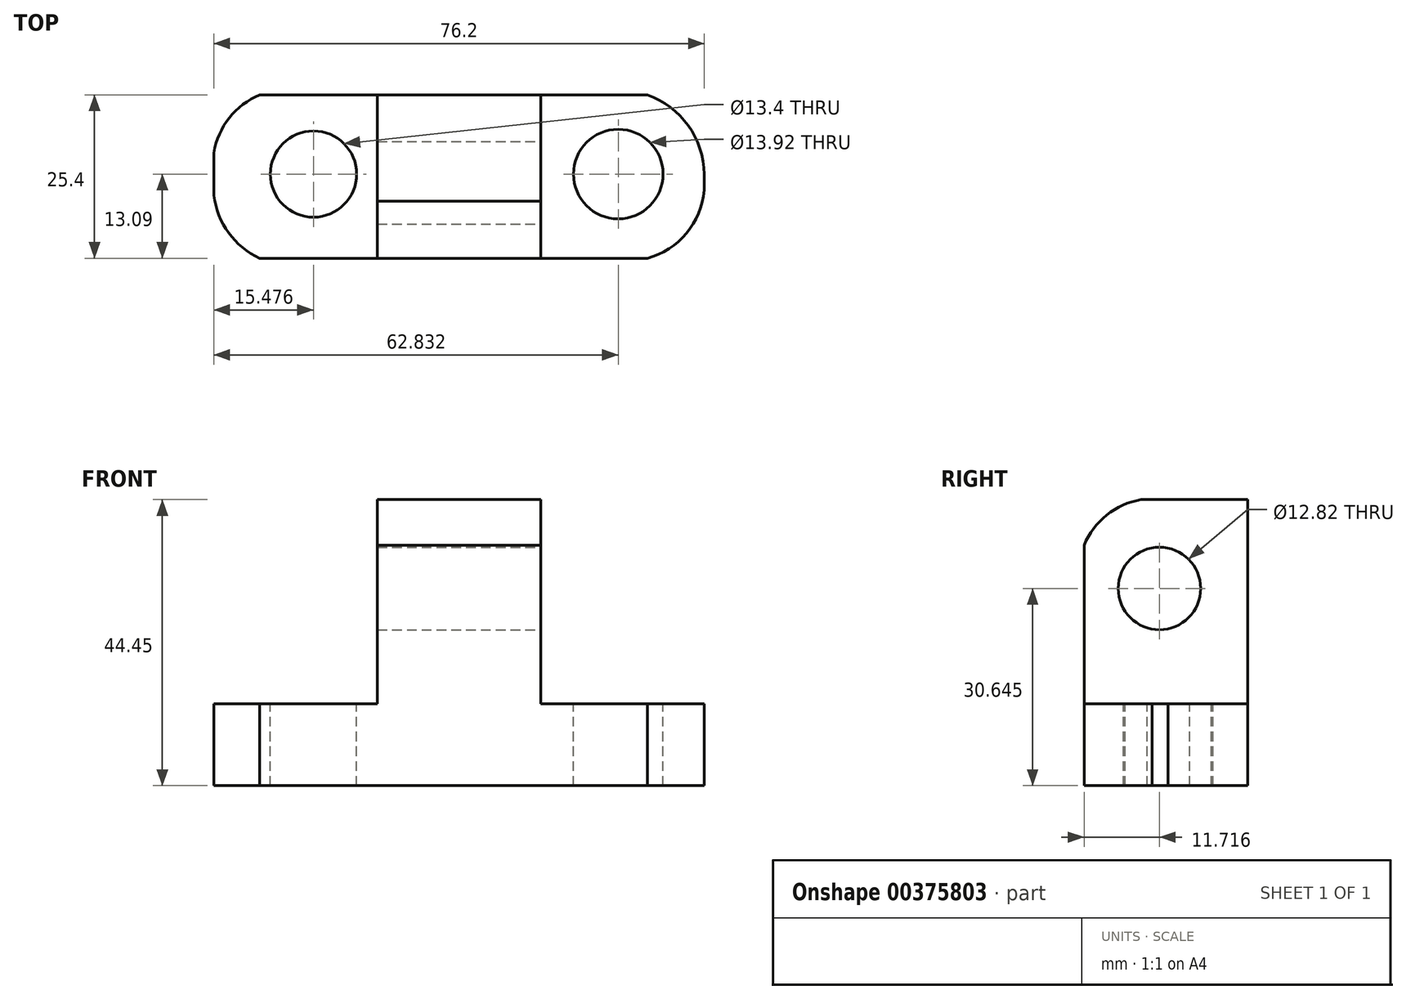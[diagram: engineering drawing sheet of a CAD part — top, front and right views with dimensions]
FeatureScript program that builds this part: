
annotation { "Feature Type Name" : "Feature", "Feature Type Description" : "" }
export const myFeature = defineFeature(function(context is Context, id is Id, definition is map)
    precondition{}
    {
        {
            var Q0;
            Q0=qCreatedBy(makeId("Front.planeOp"),FACE);
            var sketch = newSketch(context, id + "F0", { "sketchPlane" : qUnion([Q0])});
            skLineSegment(sketch, "E0", {"start": v(0, 0) * mm, "end": v(76.2, 0) * mm});
            skLineSegment(sketch, "E1", {"start": v(76.2, 0) * mm, "end": v(76.2, 44.45) * mm});
            skLineSegment(sketch, "E2", {"start": v(76.2, 44.45) * mm, "end": v(0, 44.45) * mm});
            skLineSegment(sketch, "E3", {"start": v(0, 44.45) * mm, "end": v(0, 0) * mm});
            skSolve(sketch);
        }
        {
            var Q0;
            Q0 = qSketchRegion(id + "F0", true);
            var Q1;
            Q1=makeQuery(id+"F0.imprint","IMPRINT",FACE,{"disambiguationData":[TD([[makeQuery(id+"F0.imprint","IMPRINT",EDGE,{"derivedFrom":sQuery(id+"F0.wireOp",EDGE,"E0")}),1.0]])]});
            extrude(context, id + "F1", {"entities" : qUnion([Q0, Q1]), "depth" : 25.4 * mm});
        }
        {
            var Q0;
            Q0=makeQuery(id+"F1.opExtrude","CAP_FACE",FACE,{"disambiguationData":[OSD([sQuery(id+"F0.wireOp",EDGE,"E0"),sQuery(id+"F0.wireOp",EDGE,"E1"),sQuery(id+"F0.wireOp",EDGE,"E2"),sQuery(id+"F0.wireOp",EDGE,"E3")])],"isStart":false});
            var sketch = newSketch(context, id + "F2", { "sketchPlane" : qUnion([Q0])});
            skLineSegment(sketch, "E4", {"start": v(0, 12.7) * mm, "end": v(25.4, 12.7) * mm});
            skLineSegment(sketch, "E5", {"start": v(0, 12.7) * mm, "end": v(0, 44.45) * mm});
            skLineSegment(sketch, "E6", {"start": v(0, 44.45) * mm, "end": v(25.4, 44.45) * mm});
            skLineSegment(sketch, "E7", {"start": v(25.4, 44.45) * mm, "end": v(25.4, 12.7) * mm});
            skLineSegment(sketch, "E8", {"start": v(76.2, 12.7) * mm, "end": v(50.8, 12.7) * mm});
            skLineSegment(sketch, "E9", {"start": v(50.8, 12.7) * mm, "end": v(50.8, 44.45) * mm});
            skLineSegment(sketch, "E10", {"start": v(50.8, 44.45) * mm, "end": v(76.2, 44.45) * mm});
            skLineSegment(sketch, "E11", {"start": v(76.2, 44.45) * mm, "end": v(76.2, 12.7) * mm});
            skSolve(sketch);
        }
        {
            var Q0;
            Q0=makeQuery(id+"F2.imprint","IMPRINT",FACE,{"disambiguationData":[TD([[makeQuery(id+"F2.imprint","IMPRINT",EDGE,{"derivedFrom":sQuery(id+"F2.wireOp",EDGE,"E4")}),1.0]])]});
            var Q1;
            Q1=makeQuery(id+"F2.imprint","IMPRINT",FACE,{"disambiguationData":[TD([[makeQuery(id+"F2.imprint","IMPRINT",EDGE,{"derivedFrom":sQuery(id+"F2.wireOp",EDGE,"E8")}),-1.0]])]});
            extrude(context, id + "F3", {"entities" : qUnion([Q0, Q1]), "operationType" : NewBodyOperationType.REMOVE, "oppositeDirection" : true, "depth" : 25.4 * mm});
        }
        {
            var Q0;
            Q0=makeQuery(id+"F3.boolean.opBoolean","COPY",FACE,{"derivedFrom":makeQuery(id+"F3.opExtrude","SWEPT_FACE",FACE,{"disambiguationData":[OSD([sQuery(id+"F2.wireOp",EDGE,"E9")])]})});
            var sketch = newSketch(context, id + "F4", { "sketchPlane" : qUnion([Q0])});
            skArc(sketch, "E12", {"start": v(-12.7, 44.45) * mm, "mid": v(-23.7, 40.24) * mm, "end": v(-25.4, 28.58) * mm});
            skArc(sketch, "E13", {"start": v(0, 28.58) * mm, "mid": v(-2.88, 39.3) * mm, "end": v(-12.7, 44.45) * mm});
            skSolve(sketch);
        }
        {
            var Q0;
            Q0 = qSketchRegion(id + "F4", true);
            var Q1;
            {var subQ0=sQuery(id+"F4.wireOp",EDGE,"E12");var subQ1=sQuery(id+"F2.wireOp",EDGE,"E9");var subQ4=makeQuery(id+"F3.boolean.opBoolean","COPY",EDGE,{"derivedFrom":makeQuery(id+"F3.opExtrude","CAP_EDGE",EDGE,{"disambiguationData":[OSD([subQ1])],"isStart":true})});var subQ5=makeQuery(id+"F4.imprint","INTERSECT",VERTEX,{"disambiguationData":[OD(1.0)],"derivedFrom":[subQ4,subQ0]});Q1=makeQuery(id+"F4.imprint","IMPRINT",FACE,{"disambiguationData":[TD([[makeQuery(id+"F4.imprint","IMPRINT",EDGE,{"disambiguationData":[TD([[subQ5,1.0]])],"derivedFrom":subQ0}),-1.0]])]});}
            var Q2;
            {var subQ0=sQuery(id+"F4.wireOp",EDGE,"E13");var subQ1=sQuery(id+"F2.wireOp",EDGE,"E9");var subQ4=makeQuery(id+"F3.boolean.opBoolean","COPY",EDGE,{"derivedFrom":makeQuery(id+"F3.opExtrude","CAP_EDGE",EDGE,{"disambiguationData":[OSD([subQ1])],"isStart":false})});var subQ5=makeQuery(id+"F4.imprint","INTERSECT",VERTEX,{"disambiguationData":[OD(1.0)],"derivedFrom":[subQ4,subQ0]});Q2=makeQuery(id+"F4.imprint","IMPRINT",FACE,{"disambiguationData":[TD([[makeQuery(id+"F4.imprint","IMPRINT",EDGE,{"disambiguationData":[TD([[subQ5,-1.0]])],"derivedFrom":subQ4}),1.0]])]});}
            extrude(context, id + "F5", {"entities" : qUnion([Q0, Q1, Q2]), "operationType" : NewBodyOperationType.REMOVE, "oppositeDirection" : true, "depth" : 25.4 * mm});
        }
        {
            var Q0;
            Q0=makeQuery(id+"F3.boolean.opBoolean","COPY",FACE,{"derivedFrom":makeQuery(id+"F3.opExtrude","SWEPT_FACE",FACE,{"disambiguationData":[OSD([sQuery(id+"F2.wireOp",EDGE,"E9")])]})});
            var sketch = newSketch(context, id + "F6", { "sketchPlane" : qUnion([Q0])});
            skCircle(sketch, "E14", {"center": v(-13.68, 30.65) * mm, "radius": 6.4 * mm});
            skSolve(sketch);
        }
        {
            var Q0;
            Q0=makeQuery(id+"F6.imprint","IMPRINT",FACE,{"disambiguationData":[TD([[makeQuery(id+"F6.imprint","IMPRINT",EDGE,{"derivedFrom":sQuery(id+"F6.wireOp",EDGE,"E14")}),1.0]])]});
            extrude(context, id + "F7", {"entities" : qUnion([Q0]), "operationType" : NewBodyOperationType.REMOVE, "oppositeDirection" : true, "depth" : 25.4 * mm});
        }
        {
            var Q0;
            Q0=makeQuery(id+"F3.boolean.opBoolean","COPY",FACE,{"derivedFrom":makeQuery(id+"F3.opExtrude","SWEPT_FACE",FACE,{"disambiguationData":[OSD([sQuery(id+"F2.wireOp",EDGE,"E4")])]})});
            var sketch = newSketch(context, id + "F8", { "sketchPlane" : qUnion([Q0])});
            skArc(sketch, "E15", {"start": v(0, -12.7) * mm, "mid": v(1.5, -20.2) * mm, "end": v(7.12, -25.4) * mm});
            skArc(sketch, "E16", {"start": v(7.12, 0) * mm, "mid": v(1.35, -5.11) * mm, "end": v(0, -12.7) * mm});
            skPoint(sketch, "E16.startSnap0", {"position": v(12.7, 0) * mm});
            skSolve(sketch);
        }
        {
            var Q0;
            Q0 = qSketchRegion(id + "F8", true);
            var Q1;
            {var subQ0=sQuery(id+"F8.wireOp",EDGE,"E16");var subQ1=sQuery(id+"F2.wireOp",EDGE,"E4");var subQ2=makeQuery(id+"F3.boolean.opBoolean","COPY",EDGE,{"derivedFrom":makeQuery(id+"F3.opExtrude","CAP_EDGE",EDGE,{"disambiguationData":[OSD([subQ1])],"isStart":false})});var subQ3=makeQuery(id+"F8.imprint","INTERSECT",VERTEX,{"derivedFrom":[subQ2,subQ0]});Q1=makeQuery(id+"F8.imprint","IMPRINT",FACE,{"disambiguationData":[TD([[makeQuery(id+"F8.imprint","IMPRINT",EDGE,{"disambiguationData":[TD([[subQ3,-1.0]])],"derivedFrom":subQ0}),-1.0]])]});}
            var Q2;
            {var subQ0=sQuery(id+"F8.wireOp",EDGE,"E15");var subQ1=sQuery(id+"F2.wireOp",EDGE,"E4");var subQ2=makeQuery(id+"F3.boolean.opBoolean","COPY",EDGE,{"derivedFrom":makeQuery(id+"F3.opExtrude","CAP_EDGE",EDGE,{"disambiguationData":[OSD([subQ1])],"isStart":true})});var subQ3=makeQuery(id+"F8.imprint","INTERSECT",VERTEX,{"derivedFrom":[subQ2,subQ0]});Q2=makeQuery(id+"F8.imprint","IMPRINT",FACE,{"disambiguationData":[TD([[makeQuery(id+"F8.imprint","IMPRINT",EDGE,{"disambiguationData":[TD([[subQ3,1.0]])],"derivedFrom":subQ0}),-1.0]])]});}
            extrude(context, id + "F9", {"entities" : qUnion([Q0, Q1, Q2]), "operationType" : NewBodyOperationType.REMOVE, "oppositeDirection" : true, "depth" : 25.4 * mm});
        }
        {
            var Q0;
            Q0=makeQuery(id+"F3.boolean.opBoolean","COPY",FACE,{"derivedFrom":makeQuery(id+"F3.opExtrude","SWEPT_FACE",FACE,{"disambiguationData":[OSD([sQuery(id+"F2.wireOp",EDGE,"E8")])]})});
            var sketch = newSketch(context, id + "F10", { "sketchPlane" : qUnion([Q0])});
            skArc(sketch, "E17", {"start": v(67.34, -25.4) * mm, "mid": v(74.08, -20.66) * mm, "end": v(76.2, -12.7) * mm});
            skArc(sketch, "E18", {"start": v(76.2, -12.7) * mm, "mid": v(73.81, -4.92) * mm, "end": v(67.34, 0) * mm});
            skSolve(sketch);
        }
        {
            var Q0;
            {var subQ0=sQuery(id+"F10.wireOp",EDGE,"E18");var subQ1=sQuery(id+"F2.wireOp",EDGE,"E8");var subQ2=makeQuery(id+"F3.boolean.opBoolean","COPY",EDGE,{"derivedFrom":makeQuery(id+"F3.opExtrude","CAP_EDGE",EDGE,{"disambiguationData":[OSD([subQ1])],"isStart":false})});var subQ3=makeQuery(id+"F10.imprint","INTERSECT",VERTEX,{"derivedFrom":[subQ2,subQ0]});Q0=makeQuery(id+"F10.imprint","IMPRINT",FACE,{"disambiguationData":[TD([[makeQuery(id+"F10.imprint","IMPRINT",EDGE,{"disambiguationData":[TD([[subQ3,1.0]])],"derivedFrom":subQ0}),-1.0]])]});}
            var Q1;
            {var subQ0=sQuery(id+"F10.wireOp",EDGE,"E17");var subQ1=sQuery(id+"F2.wireOp",EDGE,"E8");var subQ2=makeQuery(id+"F3.boolean.opBoolean","COPY",EDGE,{"derivedFrom":makeQuery(id+"F3.opExtrude","CAP_EDGE",EDGE,{"disambiguationData":[OSD([subQ1])],"isStart":true})});var subQ3=makeQuery(id+"F10.imprint","INTERSECT",VERTEX,{"derivedFrom":[subQ2,subQ0]});Q1=makeQuery(id+"F10.imprint","IMPRINT",FACE,{"disambiguationData":[TD([[makeQuery(id+"F10.imprint","IMPRINT",EDGE,{"disambiguationData":[TD([[subQ3,-1.0]])],"derivedFrom":subQ0}),-1.0]])]});}
            extrude(context, id + "F11", {"entities" : qUnion([Q0, Q1]), "operationType" : NewBodyOperationType.REMOVE, "oppositeDirection" : true, "depth" : 25.4 * mm});
        }
        {
            var Q0;
            Q0=makeQuery(id+"F3.boolean.opBoolean","COPY",FACE,{"derivedFrom":makeQuery(id+"F3.opExtrude","SWEPT_FACE",FACE,{"disambiguationData":[OSD([sQuery(id+"F2.wireOp",EDGE,"E4")])]})});
            var sketch = newSketch(context, id + "F12", { "sketchPlane" : qUnion([Q0])});
            skCircle(sketch, "E19", {"center": v(15.48, -12.31) * mm, "radius": 6.7 * mm});
            skPoint(sketch, "E19.centerSnap0", {"position": v(0, -12.31) * mm});
            skCircle(sketch, "E20", {"center": v(62.83, -12.31) * mm, "radius": 6.96 * mm});
            skSolve(sketch);
        }
        {
            var Q0;
            Q0=makeQuery(id+"F12.imprint","IMPRINT",FACE,{"disambiguationData":[TD([[makeQuery(id+"F12.imprint","IMPRINT",EDGE,{"derivedFrom":sQuery(id+"F12.wireOp",EDGE,"E20")}),1.0]])]});
            var Q1;
            Q1=makeQuery(id+"F12.imprint","IMPRINT",FACE,{"disambiguationData":[TD([[makeQuery(id+"F12.imprint","IMPRINT",EDGE,{"derivedFrom":sQuery(id+"F12.wireOp",EDGE,"E19")}),1.0]])]});
            extrude(context, id + "F13", {"entities" : qUnion([Q0, Q1]), "operationType" : NewBodyOperationType.REMOVE, "oppositeDirection" : true, "depth" : 25.4 * mm});
        }
    });
